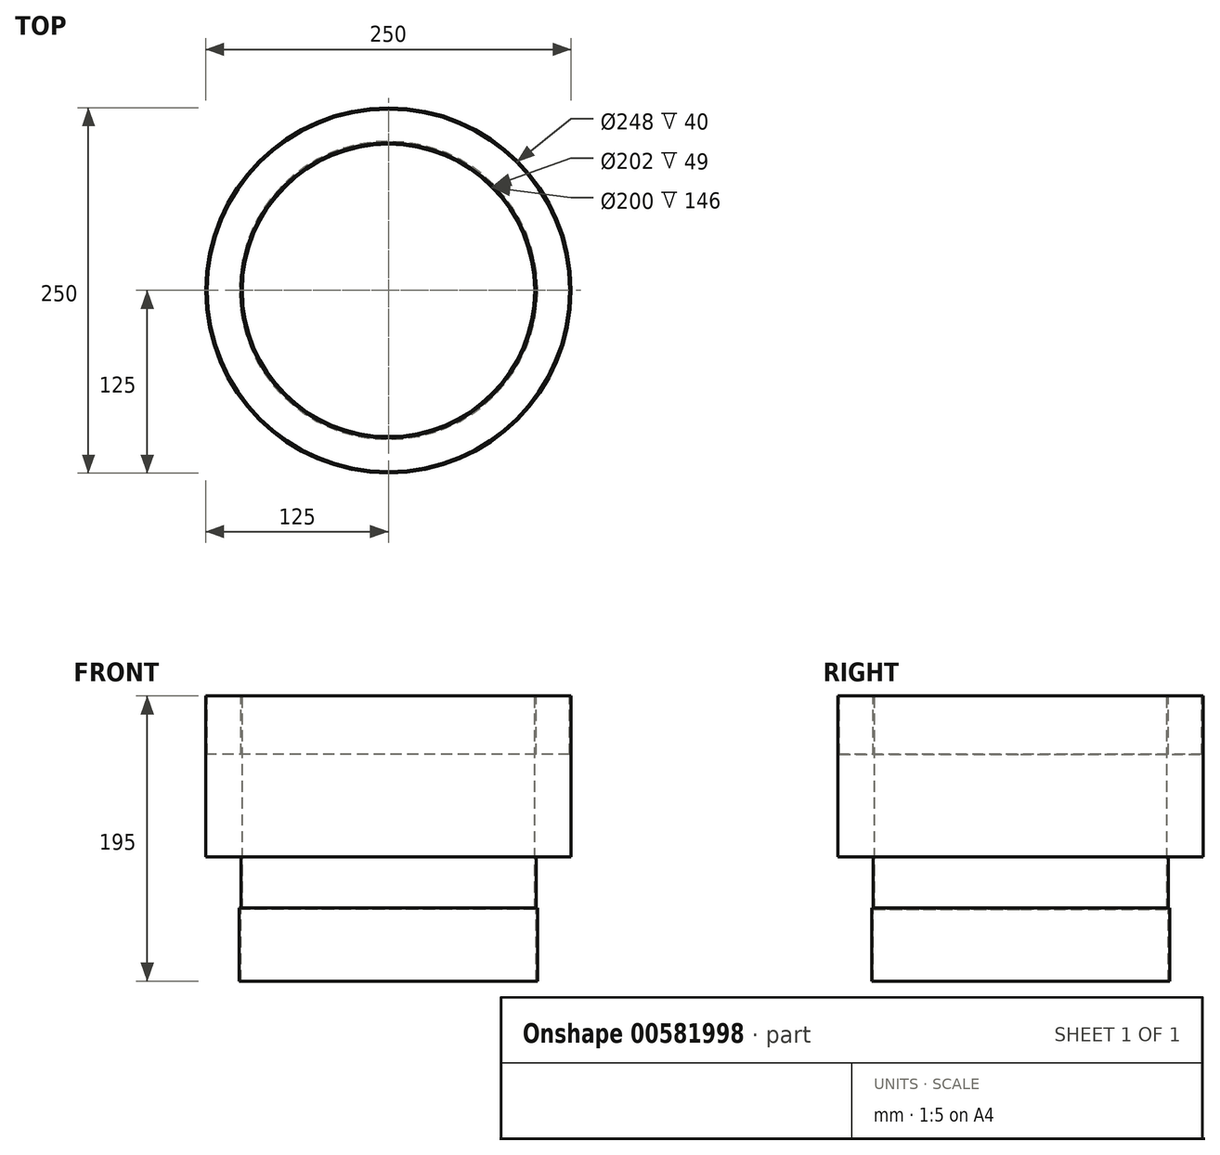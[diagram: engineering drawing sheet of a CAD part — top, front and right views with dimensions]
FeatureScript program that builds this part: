
annotation { "Feature Type Name" : "Feature", "Feature Type Description" : "" }
export const myFeature = defineFeature(function(context is Context, id is Id, definition is map)
    precondition{}
    {
        {
            var Q0;
            Q0=qCreatedBy(makeId("Front.planeOp"),FACE);
            var sketch = newSketch(context, id + "F0", { "sketchPlane" : qUnion([Q0])});
            skLineSegment(sketch, "E0", {"start": v(0, 710.75) * mm, "end": v(0, -704.58) * mm, "construction": true});
            skLineSegment(sketch, "E1", {"start": v(-100, 264.65) * mm, "end": v(-100, 410.65) * mm});
            skLineSegment(sketch, "E2", {"start": v(-100, 410.65) * mm, "end": v(-101, 410.65) * mm});
            skLineSegment(sketch, "E3", {"start": v(-124, 410.65) * mm, "end": v(-125, 410.65) * mm});
            skLineSegment(sketch, "E4", {"start": v(-125, 410.65) * mm, "end": v(-125, 300.65) * mm});
            skLineSegment(sketch, "E5", {"start": v(-125, 300.65) * mm, "end": v(-101, 300.65) * mm});
            skLineSegment(sketch, "E6", {"start": v(-101, 300.65) * mm, "end": v(-101, 265.65) * mm});
            skLineSegment(sketch, "E7", {"start": v(-124, 410.65) * mm, "end": v(-124, 370.65) * mm});
            skLineSegment(sketch, "E8", {"start": v(-124, 370.65) * mm, "end": v(-101, 370.65) * mm});
            skLineSegment(sketch, "E9", {"start": v(-101, 370.65) * mm, "end": v(-101, 410.65) * mm});
            skLineSegment(sketch, "E10", {"start": v(-101, 265.65) * mm, "end": v(-102, 265.65) * mm});
            skLineSegment(sketch, "E11", {"start": v(-102, 265.65) * mm, "end": v(-102, 215.65) * mm});
            skLineSegment(sketch, "E12", {"start": v(-102, 215.65) * mm, "end": v(-101, 215.65) * mm});
            skLineSegment(sketch, "E13", {"start": v(-100, 264.65) * mm, "end": v(-101, 264.65) * mm});
            skLineSegment(sketch, "E14", {"start": v(-101, 264.65) * mm, "end": v(-101, 215.65) * mm});
            skPoint(sketch, "E15.end.orphan", {"position": v(-100, 215.65) * mm});
            skSolve(sketch);
        }
        {
            var Q0;
            Q0=qSketchRegion(id+"F0",true);
            var Q1;
            Q1=sQuery(id+"F0.wireOp",EDGE,"E0");
            revolve(context, id + "F1", {"entities" : qUnion([Q0]), "axis" : qUnion([Q1]), "revolveType" : RevolveType.FULL});
        }
    });
